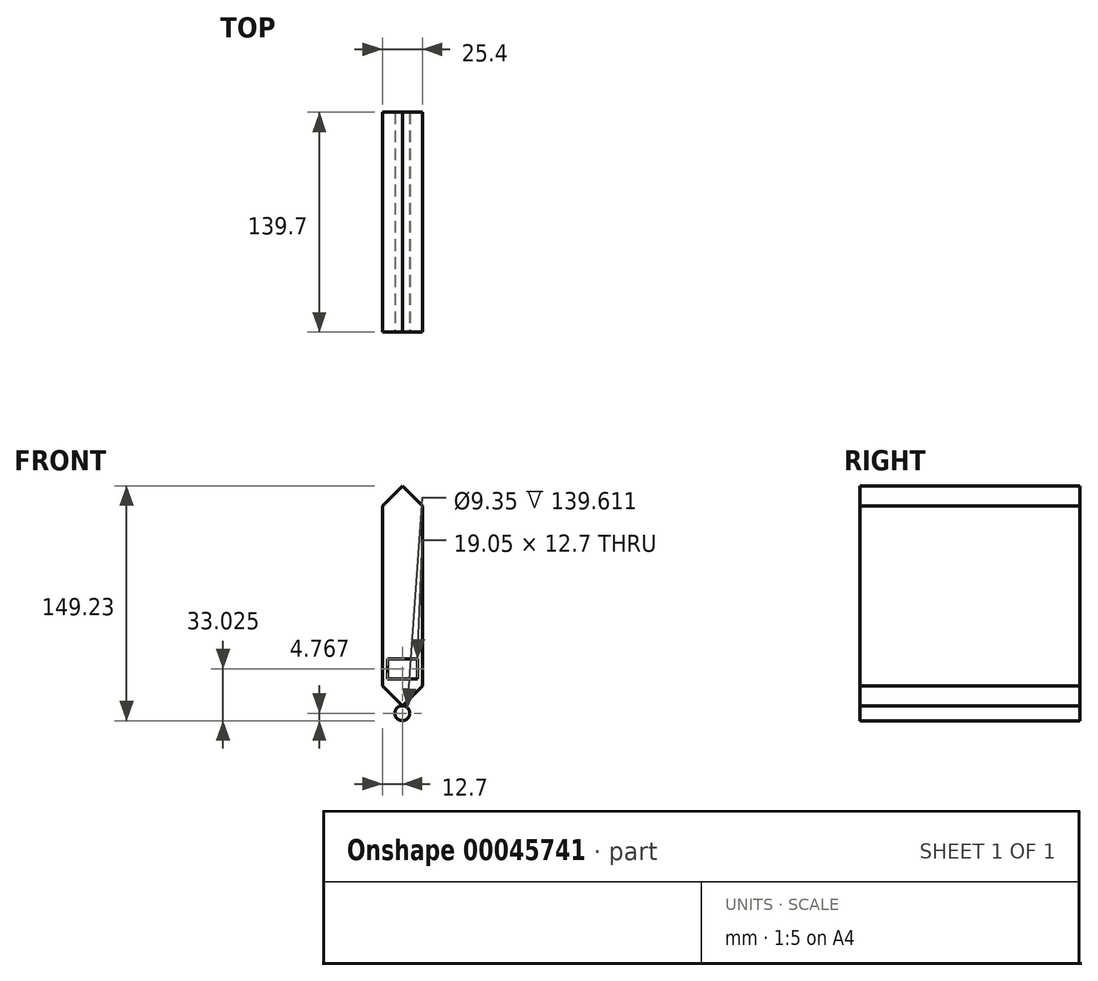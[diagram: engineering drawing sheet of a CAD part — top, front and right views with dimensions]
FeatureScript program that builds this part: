
annotation { "Feature Type Name" : "Feature", "Feature Type Description" : "" }
export const myFeature = defineFeature(function(context is Context, id is Id, definition is map)
    precondition{}
    {
        {
            var Q0;
            Q0=qCreatedBy(makeId("Front.planeOp"),FACE);
            var sketch = newSketch(context, id + "F0", { "sketchPlane" : qUnion([Q0])});
            skLineSegment(sketch, "E0", {"start": v(0, 0) * mm, "end": v(12.7, 12.7) * mm});
            skLineSegment(sketch, "E1", {"start": v(12.7, 12.7) * mm, "end": v(12.7, 127) * mm});
            skLineSegment(sketch, "E2", {"start": v(12.7, 127) * mm, "end": v(0, 139.7) * mm});
            skLineSegment(sketch, "E3.MirrorCS", {"start": v(0, 0) * mm, "end": v(-12.7, 12.7) * mm});
            skLineSegment(sketch, "E4.MirrorCS", {"start": v(-12.7, 12.7) * mm, "end": v(-12.7, 127) * mm});
            skLineSegment(sketch, "E5.MirrorCS", {"start": v(-12.7, 127) * mm, "end": v(0, 139.7) * mm});
            skLineSegment(sketch, "E6.bottom", {"start": v(-9.53, 29.85) * mm, "end": v(9.53, 29.85) * mm});
            skLineSegment(sketch, "E6.top", {"start": v(-9.53, 17.15) * mm, "end": v(9.53, 17.15) * mm});
            skLineSegment(sketch, "E6.left", {"start": v(-9.53, 29.85) * mm, "end": v(-9.53, 17.15) * mm});
            skLineSegment(sketch, "E6.right", {"start": v(9.52, 29.85) * mm, "end": v(9.52, 17.15) * mm});
            skPoint(sketch, "E7", {"position": v(0, 29.85) * mm});
            skSolve(sketch);
        }
        {
            var Q0;
            Q0 = qSketchRegion(id + "F0", true);
            var Q1;
            Q1=makeQuery(id+"F0.imprint","IMPRINT",FACE,{"disambiguationData":[TD([[makeQuery(id+"F0.imprint","IMPRINT",EDGE,{"derivedFrom":sQuery(id+"F0.wireOp",EDGE,"E6.bottom")}),-1.0]])]});
            extrude(context, id + "F1", {"entities" : qUnion([Q0, Q1]), "oppositeDirection" : true, "depth" : 139.7 * mm});
        }
        {
            var Q0;
            Q0=qCreatedBy(makeId("Front.planeOp"),FACE);
            var sketch = newSketch(context, id + "F2", { "sketchPlane" : qUnion([Q0])});
            skCircle(sketch, "E8", {"center": v(0, -4.76) * mm, "radius": 4.76 * mm});
            skSolve(sketch);
        }
        {
            var Q0;
            Q0 = qSketchRegion(id + "F2", true);
            var Q1;
            Q1=makeQuery(id+"F1.opExtrude","CAP_FACE",FACE,{"disambiguationData":[OSD([sQuery(id+"F0.wireOp",EDGE,"E0"),sQuery(id+"F0.wireOp",EDGE,"E1"),sQuery(id+"F0.wireOp",EDGE,"E2"),sQuery(id+"F0.wireOp",EDGE,"E3.MirrorCS"),sQuery(id+"F0.wireOp",EDGE,"E4.MirrorCS"),sQuery(id+"F0.wireOp",EDGE,"E5.MirrorCS")])],"isStart":false});
            extrude(context, id + "F3", {"entities" : qUnion([Q0]), "endBound" : BoundingType.UP_TO_SURFACE, "oppositeDirection" : true, "endBoundEntityFace" : qUnion([Q1]), "depth" : 25.4 * mm});
        }
        {
            var Q0;
            Q0=makeQuery(id+"F1.opExtrude","CAP_FACE",FACE,{"disambiguationData":[OSD([sQuery(id+"F0.wireOp",EDGE,"E0"),sQuery(id+"F0.wireOp",EDGE,"E1"),sQuery(id+"F0.wireOp",EDGE,"E2"),sQuery(id+"F0.wireOp",EDGE,"E3.MirrorCS"),sQuery(id+"F0.wireOp",EDGE,"E4.MirrorCS"),sQuery(id+"F0.wireOp",EDGE,"E5.MirrorCS"),sQuery(id+"F0.wireOp",EDGE,"E6.bottom"),sQuery(id+"F0.wireOp",EDGE,"E6.top"),sQuery(id+"F0.wireOp",EDGE,"E6.left"),sQuery(id+"F0.wireOp",EDGE,"E6.right")])],"isStart":false});
            var Q1;
            Q1=makeQuery(id+"F3.opExtrude","CAP_FACE",FACE,{"disambiguationData":[OSD([sQuery(id+"F2.wireOp",EDGE,"E8")])],"isStart":false});
            shell(context, id + "F4", {"entities" : qUnion([Q0, Q1]), "thickness" : 0.09 * mm});
        }
        {
            var Q0;
            Q0=makeQuery(id+"F0.imprint","IMPRINT",FACE,{"disambiguationData":[TD([[makeQuery(id+"F0.imprint","IMPRINT",EDGE,{"derivedFrom":sQuery(id+"F0.wireOp",EDGE,"E6.bottom")}),-1.0]])]});
            extrude(context, id + "F5", {"entities" : qUnion([Q0]), "operationType" : NewBodyOperationType.REMOVE, "endBound" : BoundingType.UP_TO_NEXT, "oppositeDirection" : true, "depth" : 25.4 * mm});
        }
    });
